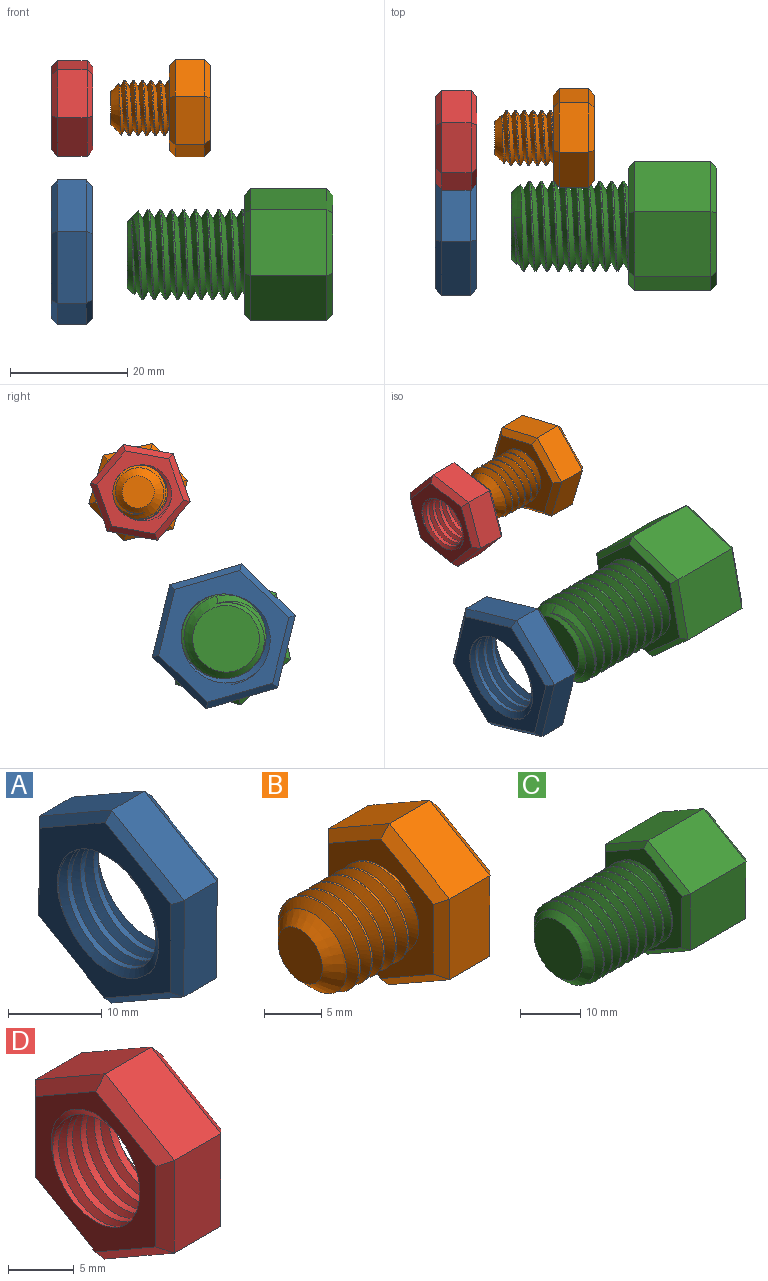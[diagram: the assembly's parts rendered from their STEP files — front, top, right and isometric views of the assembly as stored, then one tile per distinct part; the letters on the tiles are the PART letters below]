
ASSEMBLY  parts=4 mates=2
PART A: 23 faces, bbox 9.3x22.7x26 mm
  f0: cylinder r=7.24mm len=14.48mm, axis (1,0,0), area 111.6mm2, adj f7,f8,f21,f22
  f1: plane 10.98x6.38mm, normal (0,-0.5,0.86), area 63.5mm2, adj f2,f6,f14,f18
  f2: plane 12.7x5mm, normal (0,-1,0), area 63.5mm2, adj f1,f3,f12,f16
  f3: plane 11.02x6.32mm, normal (0,-0.5,-0.87), area 63.5mm2, adj f2,f4,f10,f15
  f4: plane 10.98x6.38mm, normal (0,0.5,-0.86), area 63.5mm2, adj f3,f5,f9,f17
  f5: plane 12.7x5mm, normal (0,1,0), area 63.5mm2, adj f4,f6,f11,f19
  f6: plane 11.02x6.32mm, normal (0,0.5,0.87), area 63.5mm2, adj f1,f5,f13,f20
  f7: plane 23.73x20.67mm, normal (-1,0,0), area 164.4mm2, adj f0,f9,f10,f11,f12,f13,f14,f21
  f8: plane 23.73x20.67mm, normal (1,0,0), area 164.4mm2, adj f0,f15,f16,f17,f18,f19,f20,f21
  f9: plane 10.99x6.96mm, normal (-0.71,0.36,-0.61), area 17.1mm2, adj f4,f7,f10,f11
  f10: plane 11.02x6.9mm, normal (-0.71,-0.35,-0.61), area 17.1mm2, adj f3,f7,f9,f12
  f11: plane 12.7x1.03mm, normal (-0.71,0.71,0), area 17.1mm2, adj f5,f7,f9,f13
  f12: plane 12.7x1.03mm, normal (-0.71,-0.71,0), area 17.1mm2, adj f2,f7,f10,f14
  f13: plane 11.02x6.9mm, normal (-0.71,0.35,0.61), area 17.1mm2, adj f6,f7,f11,f14
  f14: plane 10.99x6.96mm, normal (-0.71,-0.36,0.61), area 17.1mm2, adj f1,f7,f12,f13
  f15: plane 11.02x6.9mm, normal (0.71,-0.35,-0.61), area 17.1mm2, adj f3,f8,f16,f17
  f16: plane 12.7x1.03mm, normal (0.71,-0.71,0), area 17.1mm2, adj f2,f8,f15,f18
  f17: plane 10.99x6.96mm, normal (0.71,0.36,-0.61), area 17.1mm2, adj f4,f8,f15,f19
  f18: plane 10.99x6.96mm, normal (0.71,-0.36,0.61), area 17.1mm2, adj f1,f8,f16,f20
  f19: plane 12.7x1.03mm, normal (0.71,0.71,0), area 17.1mm2, adj f5,f8,f17,f20
  f20: plane 11.02x6.9mm, normal (0.71,0.35,0.61), area 17.1mm2, adj f6,f8,f18,f19
  f21: bspline ~19.31x16.73mm, area 223mm2, adj f0,f7,f8,f22
  f22: bspline ~19.31x16.73mm, area 223mm2, adj f0,f7,f8,f21
PART B: 25 faces, bbox 17.8x15.9x18.1 mm
  f0: cylinder r=4.75mm len=9.5mm, axis (1,0,0), area 28.1mm2, adj f1,f2,f4,f12
  f1: bspline ~10.97x9.91mm, area 196.7mm2, adj f0,f2,f4,f12
  f2: bspline ~10.97x10.66mm, area 196.6mm2, adj f0,f1,f4,f12
  f3: plane 5.5x5.5mm, normal (-1,0,0), area 23.8mm2, adj f4
  f4: cone r=4.75mm half-angle=45deg, axis (1,0,0), area 47.4mm2, adj f0,f1,f2,f3
  f5: plane 7.48x5mm, normal (0,-0.5,0.86), area 43.3mm2, adj f6,f10,f18,f22
  f6: plane 8.66x5mm, normal (0,-1,0), area 43.3mm2, adj f5,f7,f16,f20
  f7: plane 7.52x5mm, normal (0,-0.5,-0.87), area 43.3mm2, adj f6,f8,f14,f19
  f8: plane 7.48x5mm, normal (0,0.5,-0.86), area 43.3mm2, adj f7,f9,f13,f21
  f9: plane 8.66x5mm, normal (0,1,0), area 43.3mm2, adj f8,f10,f15,f23
  f10: plane 7.52x5mm, normal (0,0.5,0.87), area 43.3mm2, adj f5,f9,f17,f24
  f11: plane 15.01x13.03mm, normal (1,0,0), area 146.4mm2, adj f13,f14,f15,f16,f17,f18
  f12: plane 15.83x13.85mm, normal (-1,0,0), area 89.2mm2, adj f0,f1,f2,f19,f20,f21,f22,f23
  f13: plane 7.49x4.93mm, normal (0.71,0.36,-0.61), area 11.4mm2, adj f8,f11,f14,f15
  f14: plane 7.52x4.88mm, normal (0.71,-0.35,-0.61), area 11.4mm2, adj f7,f11,f13,f16
  f15: plane 8.66x1.03mm, normal (0.71,0.71,0), area 11.4mm2, adj f9,f11,f13,f17
  f16: plane 8.66x1.03mm, normal (0.71,-0.71,0), area 11.4mm2, adj f6,f11,f14,f18
  f17: plane 7.52x4.88mm, normal (0.71,0.35,0.61), area 11.4mm2, adj f10,f11,f15,f18
  f18: plane 7.49x4.93mm, normal (0.71,-0.36,0.61), area 11.4mm2, adj f5,f11,f16,f17
  f19: plane 7.52x4.88mm, normal (-0.71,-0.35,-0.61), area 11.4mm2, adj f7,f12,f20,f21
  f20: plane 8.66x1.03mm, normal (-0.71,-0.71,0), area 11.4mm2, adj f6,f12,f19,f22
  f21: plane 7.49x4.93mm, normal (-0.71,0.36,-0.61), area 11.4mm2, adj f8,f12,f19,f23
  f22: plane 7.49x4.93mm, normal (-0.71,-0.36,0.61), area 11.4mm2, adj f5,f12,f20,f24
  f23: plane 8.66x1.03mm, normal (-0.71,0.71,0), area 11.4mm2, adj f9,f12,f21,f24
  f24: plane 7.52x4.88mm, normal (-0.71,0.35,0.61), area 11.4mm2, adj f10,f12,f22,f23
PART C: 26 faces, bbox 35.7x20x23.1 mm
  f0: cylinder r=7.68mm len=18mm, axis (1,0,0), area 139.1mm2, adj f1,f2,f4,f13
  f1: bspline ~21.88x17.74mm, area 715.1mm2, adj f0,f2,f4,f5,f13
  f2: bspline ~20.88x17.74mm, area 713.8mm2, adj f0,f1,f4,f5,f13
  f3: plane 11.36x11.36mm, normal (-1,0,0), area 101.4mm2, adj f5
  f4: cone r=7.68mm half-angle=45deg, axis (1,0,0), area 13.2mm2, adj f0,f1,f2,f5
  f5: cone r=7.68mm half-angle=45deg, axis (1,0,0), area 63.2mm2, adj f1,f2,f3,f4
  f6: plane 13x10.02mm, normal (0,0.5,0.87), area 150.1mm2, adj f7,f11,f18,f25
  f7: plane 13x9.98mm, normal (0,-0.5,0.86), area 150.1mm2, adj f6,f8,f19,f23
  f8: plane 13x11.55mm, normal (0,-1,0), area 150.1mm2, adj f7,f9,f17,f21
  f9: plane 13x10.02mm, normal (0,-0.5,-0.87), area 150.1mm2, adj f8,f10,f15,f20
  f10: plane 13x9.98mm, normal (0,0.5,-0.86), area 150.1mm2, adj f9,f11,f14,f22
  f11: plane 13x11.55mm, normal (0,1,0), area 150.1mm2, adj f6,f10,f16,f24
  f12: plane 20.78x18.04mm, normal (1,0,0), area 280.6mm2, adj f14,f15,f16,f17,f18,f19
  f13: plane 20.78x18.04mm, normal (-1,0,0), area 125.2mm2, adj f0,f1,f2,f20,f21,f22,f23,f24
  f14: plane 9.98x6.38mm, normal (0.71,0.36,-0.61), area 15.5mm2, adj f10,f12,f15,f16
  f15: plane 10.02x6.32mm, normal (0.71,-0.35,-0.61), area 15.5mm2, adj f9,f12,f14,f17
  f16: plane 11.55x1.04mm, normal (0.71,0.71,0), area 15.5mm2, adj f11,f12,f14,f18
  f17: plane 11.55x1.04mm, normal (0.71,-0.71,0), area 15.5mm2, adj f8,f12,f15,f19
  f18: plane 10.02x6.32mm, normal (0.71,0.35,0.61), area 15.5mm2, adj f6,f12,f16,f19
  f19: plane 9.98x6.38mm, normal (0.71,-0.36,0.61), area 15.5mm2, adj f7,f12,f17,f18
  f20: plane 10.02x6.32mm, normal (-0.71,-0.35,-0.61), area 15.5mm2, adj f9,f13,f21,f22
  f21: plane 11.55x1.04mm, normal (-0.71,-0.71,0), area 15.5mm2, adj f8,f13,f20,f23
  f22: plane 9.98x6.38mm, normal (-0.71,0.36,-0.61), area 15.5mm2, adj f10,f13,f20,f24
  f23: plane 9.98x6.38mm, normal (-0.71,-0.36,0.61), area 15.5mm2, adj f7,f13,f21,f25
  f24: plane 11.55x1.04mm, normal (-0.71,0.71,0), area 15.5mm2, adj f11,f13,f22,f25
  f25: plane 10.02x6.32mm, normal (-0.71,0.35,0.61), area 15.5mm2, adj f6,f13,f23,f24
PART D: 23 faces, bbox 9.1x15.4x17.7 mm
  f0: plane 7.49x5mm, normal (0,-0.5,0.86), area 43.3mm2, adj f1,f5,f13,f17
  f1: plane 8.66x5mm, normal (0,-1,0), area 43.3mm2, adj f0,f2,f11,f15
  f2: plane 7.51x5mm, normal (0,-0.5,-0.87), area 43.3mm2, adj f1,f3,f9,f14
  f3: plane 7.49x5mm, normal (0,0.5,-0.86), area 43.3mm2, adj f2,f4,f8,f16
  f4: plane 8.66x5mm, normal (0,1,0), area 43.3mm2, adj f3,f5,f10,f18
  f5: plane 7.51x5mm, normal (0,0.5,0.87), area 43.3mm2, adj f0,f4,f12,f19
  f6: plane 15.37x13.38mm, normal (-1,0,0), area 71.4mm2, adj f8,f9,f10,f11,f12,f13,f20,f21
  f7: plane 15.37x13.38mm, normal (1,0,0), area 71.4mm2, adj f14,f15,f16,f17,f18,f19,f20,f21
  f8: plane 7.49x4.93mm, normal (-0.71,0.36,-0.61), area 11.4mm2, adj f3,f6,f9,f10
  f9: plane 7.51x4.89mm, normal (-0.71,-0.35,-0.61), area 11.4mm2, adj f2,f6,f8,f11
  f10: plane 8.66x1.02mm, normal (-0.71,0.71,0), area 11.4mm2, adj f4,f6,f8,f12
  f11: plane 8.66x1.02mm, normal (-0.71,-0.71,0), area 11.4mm2, adj f1,f6,f9,f13
  f12: plane 7.51x4.89mm, normal (-0.71,0.35,0.61), area 11.4mm2, adj f5,f6,f10,f13
  f13: plane 7.49x4.93mm, normal (-0.71,-0.36,0.61), area 11.4mm2, adj f0,f6,f11,f12
  f14: plane 7.51x4.89mm, normal (0.71,-0.35,-0.61), area 11.4mm2, adj f2,f7,f15,f16
  f15: plane 8.66x1.02mm, normal (0.71,-0.71,0), area 11.4mm2, adj f1,f7,f14,f17
  f16: plane 7.49x4.93mm, normal (0.71,0.36,-0.61), area 11.4mm2, adj f3,f7,f14,f18
  f17: plane 7.49x4.93mm, normal (0.71,-0.36,0.61), area 11.4mm2, adj f0,f7,f15,f19
  f18: plane 8.66x1.02mm, normal (0.71,0.71,0), area 11.4mm2, adj f4,f7,f16,f19
  f19: plane 7.51x4.89mm, normal (0.71,0.35,0.61), area 11.4mm2, adj f5,f7,f17,f18
  f20: cylinder r=4.66mm len=9.32mm, axis (1,0,0), area 85.4mm2, adj f6,f7,f21,f22
  f21: bspline ~12.5x10.82mm, area 128.4mm2, adj f6,f7,f20,f22
  f22: bspline ~12.5x10.82mm, area 128.5mm2, adj f6,f7,f20,f21
PLACE A rot(axis=(0,0.6,-0.8),180deg) t=(-55.27,-6.86,23.48)mm fixed
PLACE B rot(axis=(-1,0,0),43.8deg) t=(-31.66,7.73,48.08)mm
PLACE C rot(axis=(1,0,0),167.5deg) t=(-14.77,-7.25,23.06)mm
PLACE D rot(axis=(1,0,0),100.2deg) t=(-48.16,7.38,48.02)mm fixed
MATE cylindrical C.f0 <-> A.f7  axis (-1,0,0) through (-42.27,-7.25,23.06)mm
MATE cylindrical B.f0 <-> D.f6  axis (-1,0,0) through (-45.16,7.73,48.08)mm
